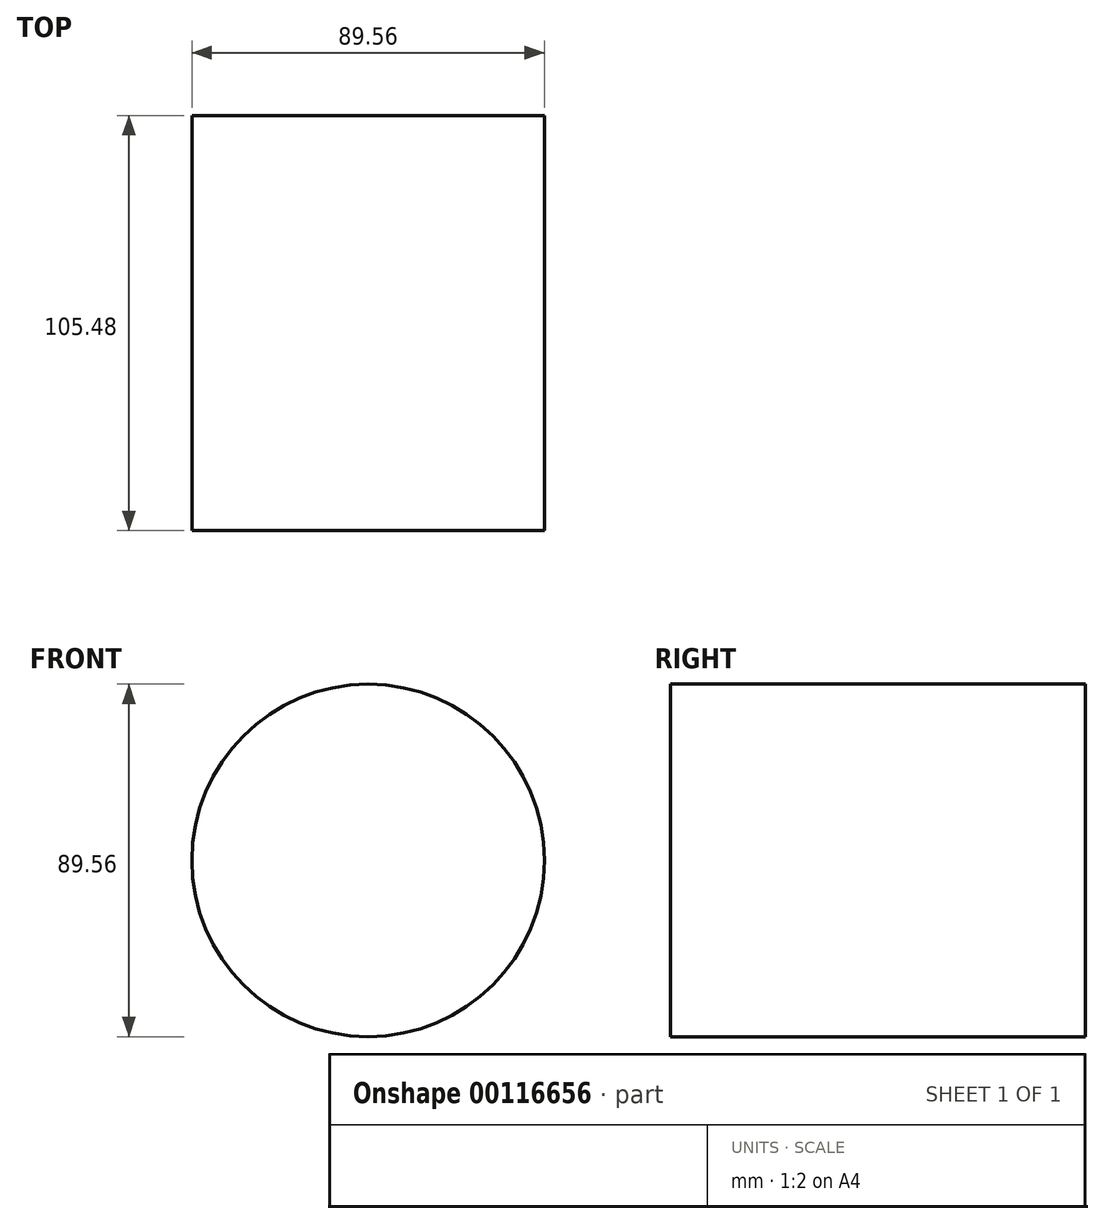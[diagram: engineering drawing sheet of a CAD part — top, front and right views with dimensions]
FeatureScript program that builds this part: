
annotation { "Feature Type Name" : "Feature", "Feature Type Description" : "" }
export const myFeature = defineFeature(function(context is Context, id is Id, definition is map)
    precondition{}
    {
        {
            var Q0;
            Q0=qCreatedBy(makeId("Front.planeOp"),FACE);
            var sketch = newSketch(context, id + "F0", { "sketchPlane" : qUnion([Q0])});
            skCircle(sketch, "E0", {"center": v(0, 0) * mm, "radius": 44.78 * mm});
            skSolve(sketch);
        }
        {
            var Q0;
            Q0 = qSketchRegion(id + "F0", true);
            extrude(context, id + "F1", {"entities" : qUnion([Q0]), "depth" : 105.48 * mm});
        }
    });
